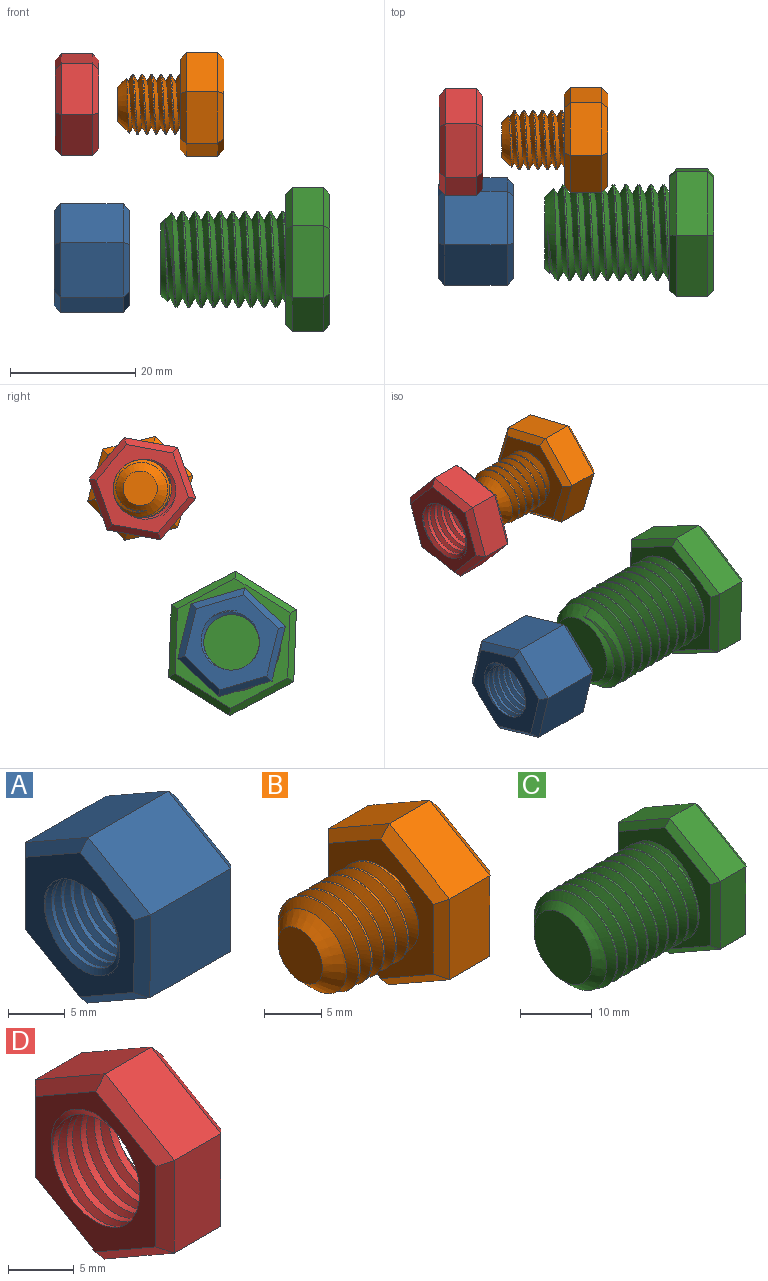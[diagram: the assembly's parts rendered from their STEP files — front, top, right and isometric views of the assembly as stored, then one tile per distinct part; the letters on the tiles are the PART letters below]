
ASSEMBLY  parts=4 mates=2
PART A: 23 faces, bbox 13.4x15.9x18.3 mm
  f0: cylinder r=4.45mm len=12mm, axis (1,0,0), area 109.8mm2, adj f7,f8,f21,f22
  f1: plane 10x7.73mm, normal (0,-0.5,0.86), area 89.5mm2, adj f2,f6,f14,f18
  f2: plane 10x8.95mm, normal (0,-1,0), area 89.5mm2, adj f1,f3,f12,f16
  f3: plane 10x7.77mm, normal (0,-0.5,-0.87), area 89.5mm2, adj f2,f4,f10,f15
  f4: plane 10x7.73mm, normal (0,0.5,-0.86), area 89.5mm2, adj f3,f5,f9,f17
  f5: plane 10x8.95mm, normal (0,1,0), area 89.5mm2, adj f4,f6,f11,f19
  f6: plane 10x7.77mm, normal (0,0.5,0.87), area 89.5mm2, adj f1,f5,f13,f20
  f7: plane 15.97x13.91mm, normal (-1,0,0), area 89.3mm2, adj f0,f9,f10,f11,f12,f13,f14,f21
  f8: plane 15.97x13.91mm, normal (1,0,0), area 89.3mm2, adj f0,f15,f16,f17,f18,f19,f20,f21
  f9: plane 7.74x5.08mm, normal (-0.71,0.36,-0.61), area 11.8mm2, adj f4,f7,f10,f11
  f10: plane 7.77x5.03mm, normal (-0.71,-0.35,-0.61), area 11.8mm2, adj f3,f7,f9,f12
  f11: plane 8.95x1.03mm, normal (-0.71,0.71,0), area 11.8mm2, adj f5,f7,f9,f13
  f12: plane 8.95x1.03mm, normal (-0.71,-0.71,0), area 11.8mm2, adj f2,f7,f10,f14
  f13: plane 7.77x5.03mm, normal (-0.71,0.35,0.61), area 11.8mm2, adj f6,f7,f11,f14
  f14: plane 7.74x5.08mm, normal (-0.71,-0.36,0.61), area 11.8mm2, adj f1,f7,f12,f13
  f15: plane 7.77x5.03mm, normal (0.71,-0.35,-0.61), area 11.8mm2, adj f3,f8,f16,f17
  f16: plane 8.95x1.03mm, normal (0.71,-0.71,0), area 11.8mm2, adj f2,f8,f15,f18
  f17: plane 7.74x5.08mm, normal (0.71,0.36,-0.61), area 11.8mm2, adj f4,f8,f15,f19
  f18: plane 7.74x5.08mm, normal (0.71,-0.36,0.61), area 11.8mm2, adj f1,f8,f16,f20
  f19: plane 8.95x1.03mm, normal (0.71,0.71,0), area 11.8mm2, adj f5,f8,f17,f20
  f20: plane 7.77x5.03mm, normal (0.71,0.35,0.61), area 11.8mm2, adj f6,f8,f18,f19
  f21: bspline ~12.99x11.83mm, area 234mm2, adj f0,f7,f8,f22
  f22: bspline ~12.79x11.83mm, area 234mm2, adj f0,f7,f8,f21
PART B: 25 faces, bbox 17.8x15.9x18.1 mm
  f0: cylinder r=4.75mm len=9.5mm, axis (1,0,0), area 28.1mm2, adj f1,f2,f4,f12
  f1: bspline ~10.97x9.91mm, area 196.7mm2, adj f0,f2,f4,f12
  f2: bspline ~10.97x10.66mm, area 196.6mm2, adj f0,f1,f4,f12
  f3: plane 5.5x5.5mm, normal (-1,0,0), area 23.8mm2, adj f4
  f4: cone r=4.75mm half-angle=45deg, axis (1,0,0), area 47.4mm2, adj f0,f1,f2,f3
  f5: plane 7.48x5mm, normal (0,-0.5,0.86), area 43.3mm2, adj f6,f10,f18,f22
  f6: plane 8.66x5mm, normal (0,-1,0), area 43.3mm2, adj f5,f7,f16,f20
  f7: plane 7.52x5mm, normal (0,-0.5,-0.87), area 43.3mm2, adj f6,f8,f14,f19
  f8: plane 7.48x5mm, normal (0,0.5,-0.86), area 43.3mm2, adj f7,f9,f13,f21
  f9: plane 8.66x5mm, normal (0,1,0), area 43.3mm2, adj f8,f10,f15,f23
  f10: plane 7.52x5mm, normal (0,0.5,0.87), area 43.3mm2, adj f5,f9,f17,f24
  f11: plane 15.01x13.03mm, normal (1,0,0), area 146.4mm2, adj f13,f14,f15,f16,f17,f18
  f12: plane 15.83x13.85mm, normal (-1,0,0), area 89.2mm2, adj f0,f1,f2,f19,f20,f21,f22,f23
  f13: plane 7.49x4.93mm, normal (0.71,0.36,-0.61), area 11.4mm2, adj f8,f11,f14,f15
  f14: plane 7.52x4.88mm, normal (0.71,-0.35,-0.61), area 11.4mm2, adj f7,f11,f13,f16
  f15: plane 8.66x1.03mm, normal (0.71,0.71,0), area 11.4mm2, adj f9,f11,f13,f17
  f16: plane 8.66x1.03mm, normal (0.71,-0.71,0), area 11.4mm2, adj f6,f11,f14,f18
  f17: plane 7.52x4.88mm, normal (0.71,0.35,0.61), area 11.4mm2, adj f10,f11,f15,f18
  f18: plane 7.49x4.93mm, normal (0.71,-0.36,0.61), area 11.4mm2, adj f5,f11,f16,f17
  f19: plane 7.52x4.88mm, normal (-0.71,-0.35,-0.61), area 11.4mm2, adj f7,f12,f20,f21
  f20: plane 8.66x1.03mm, normal (-0.71,-0.71,0), area 11.4mm2, adj f6,f12,f19,f22
  f21: plane 7.49x4.93mm, normal (-0.71,0.36,-0.61), area 11.4mm2, adj f8,f12,f19,f23
  f22: plane 7.49x4.93mm, normal (-0.71,-0.36,0.61), area 11.4mm2, adj f5,f12,f20,f24
  f23: plane 8.66x1.03mm, normal (-0.71,0.71,0), area 11.4mm2, adj f9,f12,f21,f24
  f24: plane 7.52x4.88mm, normal (-0.71,0.35,0.61), area 11.4mm2, adj f10,f12,f22,f23
PART C: 26 faces, bbox 27.7x20x23.1 mm
  f0: cylinder r=7.68mm len=18mm, axis (1,0,0), area 139.1mm2, adj f1,f2,f5,f13
  f1: bspline ~20.88x17.74mm, area 713.8mm2, adj f0,f2,f4,f5,f13
  f2: bspline ~21.88x17.74mm, area 715.1mm2, adj f0,f1,f4,f5,f13
  f3: plane 11.36x11.36mm, normal (-1,0,0), area 101.4mm2, adj f4
  f4: cone r=7.68mm half-angle=45deg, axis (1,0,0), area 63.2mm2, adj f1,f2,f3,f5
  f5: cone r=7.68mm half-angle=45deg, axis (1,0,0), area 13.2mm2, adj f0,f1,f2,f4
  f6: plane 9.98x5.81mm, normal (0,-0.5,0.86), area 57.7mm2, adj f7,f11,f19,f23
  f7: plane 11.55x5mm, normal (0,-1,0), area 57.7mm2, adj f6,f8,f17,f21
  f8: plane 10.02x5.74mm, normal (0,-0.5,-0.87), area 57.7mm2, adj f7,f9,f15,f20
  f9: plane 9.98x5.81mm, normal (0,0.5,-0.86), area 57.7mm2, adj f8,f10,f14,f22
  f10: plane 11.55x5mm, normal (0,1,0), area 57.7mm2, adj f9,f11,f16,f24
  f11: plane 10.02x5.74mm, normal (0,0.5,0.87), area 57.7mm2, adj f6,f10,f18,f25
  f12: plane 20.78x18.04mm, normal (1,0,0), area 280.6mm2, adj f14,f15,f16,f17,f18,f19
  f13: plane 20.78x18.04mm, normal (-1,0,0), area 125.2mm2, adj f0,f1,f2,f20,f21,f22,f23,f24
  f14: plane 9.98x6.38mm, normal (0.71,0.36,-0.61), area 15.5mm2, adj f9,f12,f15,f16
  f15: plane 10.02x6.32mm, normal (0.71,-0.35,-0.61), area 15.5mm2, adj f8,f12,f14,f17
  f16: plane 11.55x1.04mm, normal (0.71,0.71,0), area 15.5mm2, adj f10,f12,f14,f18
  f17: plane 11.55x1.04mm, normal (0.71,-0.71,0), area 15.5mm2, adj f7,f12,f15,f19
  f18: plane 10.02x6.32mm, normal (0.71,0.35,0.61), area 15.5mm2, adj f11,f12,f16,f19
  f19: plane 9.98x6.38mm, normal (0.71,-0.36,0.61), area 15.5mm2, adj f6,f12,f17,f18
  f20: plane 10.02x6.32mm, normal (-0.71,-0.35,-0.61), area 15.5mm2, adj f8,f13,f21,f22
  f21: plane 11.55x1.04mm, normal (-0.71,-0.71,0), area 15.5mm2, adj f7,f13,f20,f23
  f22: plane 9.98x6.38mm, normal (-0.71,0.36,-0.61), area 15.5mm2, adj f9,f13,f20,f24
  f23: plane 9.98x6.38mm, normal (-0.71,-0.36,0.61), area 15.5mm2, adj f6,f13,f21,f25
  f24: plane 11.55x1.04mm, normal (-0.71,0.71,0), area 15.5mm2, adj f10,f13,f22,f25
  f25: plane 10.02x6.32mm, normal (-0.71,0.35,0.61), area 15.5mm2, adj f11,f13,f23,f24
PART D: 23 faces, bbox 9.1x15.4x17.7 mm
  f0: plane 7.49x5mm, normal (0,-0.5,0.86), area 43.3mm2, adj f1,f5,f13,f17
  f1: plane 8.66x5mm, normal (0,-1,0), area 43.3mm2, adj f0,f2,f11,f15
  f2: plane 7.51x5mm, normal (0,-0.5,-0.87), area 43.3mm2, adj f1,f3,f9,f14
  f3: plane 7.49x5mm, normal (0,0.5,-0.86), area 43.3mm2, adj f2,f4,f8,f16
  f4: plane 8.66x5mm, normal (0,1,0), area 43.3mm2, adj f3,f5,f10,f18
  f5: plane 7.51x5mm, normal (0,0.5,0.87), area 43.3mm2, adj f0,f4,f12,f19
  f6: plane 15.37x13.38mm, normal (-1,0,0), area 71.4mm2, adj f8,f9,f10,f11,f12,f13,f20,f21
  f7: plane 15.37x13.38mm, normal (1,0,0), area 71.4mm2, adj f14,f15,f16,f17,f18,f19,f20,f21
  f8: plane 7.49x4.93mm, normal (-0.71,0.36,-0.61), area 11.4mm2, adj f3,f6,f9,f10
  f9: plane 7.51x4.89mm, normal (-0.71,-0.35,-0.61), area 11.4mm2, adj f2,f6,f8,f11
  f10: plane 8.66x1.02mm, normal (-0.71,0.71,0), area 11.4mm2, adj f4,f6,f8,f12
  f11: plane 8.66x1.02mm, normal (-0.71,-0.71,0), area 11.4mm2, adj f1,f6,f9,f13
  f12: plane 7.51x4.89mm, normal (-0.71,0.35,0.61), area 11.4mm2, adj f5,f6,f10,f13
  f13: plane 7.49x4.93mm, normal (-0.71,-0.36,0.61), area 11.4mm2, adj f0,f6,f11,f12
  f14: plane 7.51x4.89mm, normal (0.71,-0.35,-0.61), area 11.4mm2, adj f2,f7,f15,f16
  f15: plane 8.66x1.02mm, normal (0.71,-0.71,0), area 11.4mm2, adj f1,f7,f14,f17
  f16: plane 7.49x4.93mm, normal (0.71,0.36,-0.61), area 11.4mm2, adj f3,f7,f14,f18
  f17: plane 7.49x4.93mm, normal (0.71,-0.36,0.61), area 11.4mm2, adj f0,f7,f15,f19
  f18: plane 8.66x1.02mm, normal (0.71,0.71,0), area 11.4mm2, adj f4,f7,f16,f19
  f19: plane 7.51x4.89mm, normal (0.71,0.35,0.61), area 11.4mm2, adj f5,f7,f17,f18
  f20: cylinder r=4.66mm len=9.32mm, axis (1,0,0), area 85.4mm2, adj f6,f7,f21,f22
  f21: bspline ~12.5x10.82mm, area 128.4mm2, adj f6,f7,f20,f22
  f22: bspline ~12.5x10.82mm, area 128.5mm2, adj f6,f7,f20,f21
PLACE A rot(axis=(0,0.6,-0.8),180deg) t=(-55.27,-6.86,23.48)mm fixed
PLACE B rot(axis=(-1,0,0),43.8deg) t=(-31.66,7.73,48.08)mm
PLACE C rot(axis=(-1,0,0),178.1deg) t=(-14.77,-7.02,23.31)mm
PLACE D rot(axis=(1,0,0),100.2deg) t=(-48.16,7.38,48.02)mm fixed
MATE cylindrical C.f0 <-> A.f7  axis (-1,0,0) through (-38.27,-7.02,23.31)mm
MATE cylindrical B.f0 <-> D.f6  axis (-1,0,0) through (-45.16,7.73,48.08)mm
